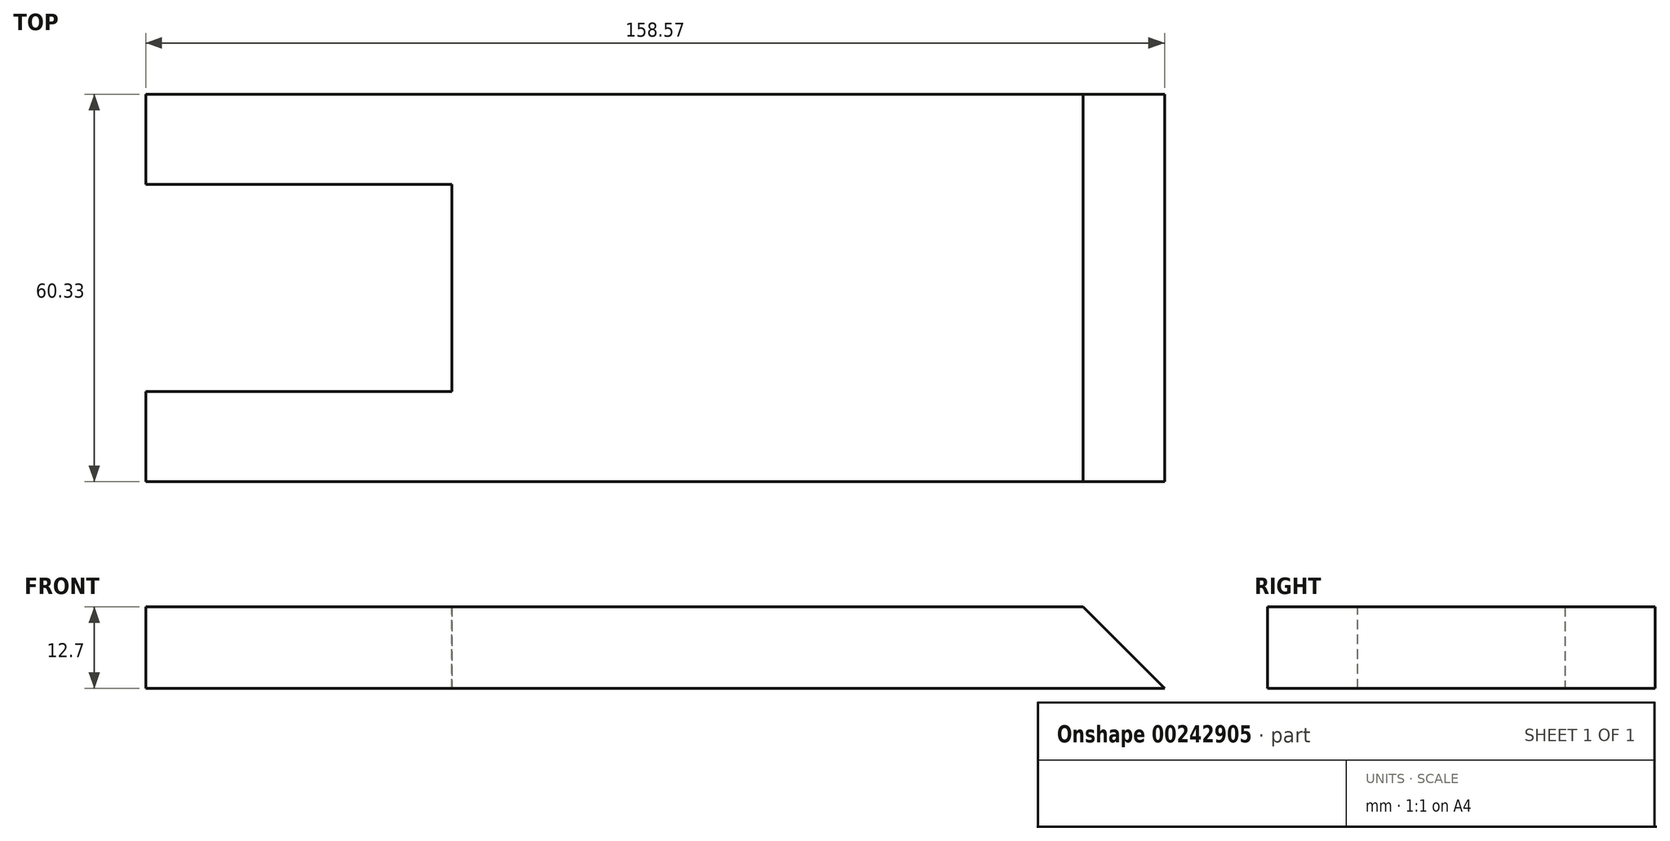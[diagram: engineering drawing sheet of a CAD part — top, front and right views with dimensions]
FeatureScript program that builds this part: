
annotation { "Feature Type Name" : "Feature", "Feature Type Description" : "" }
export const myFeature = defineFeature(function(context is Context, id is Id, definition is map)
    precondition{}
    {
        {
            var Q0;
            Q0=qCreatedBy(makeId("Top.planeOp"),FACE);
            var sketch = newSketch(context, id + "F0", { "sketchPlane" : qUnion([Q0])});
            skLineSegment(sketch, "E0", {"start": v(0, 0) * mm, "end": v(0, 14.3) * mm});
            skLineSegment(sketch, "E1", {"start": v(0, 14.3) * mm, "end": v(47.63, 14.3) * mm});
            skLineSegment(sketch, "E2", {"start": v(47.63, 14.3) * mm, "end": v(47.63, 46.04) * mm});
            skLineSegment(sketch, "E3", {"start": v(47.63, 46.04) * mm, "end": v(0, 46.04) * mm});
            skLineSegment(sketch, "E4", {"start": v(0, 46.04) * mm, "end": v(0, 60.33) * mm});
            skLineSegment(sketch, "E5", {"start": v(0, 60.33) * mm, "end": v(158.57, 60.33) * mm});
            skLineSegment(sketch, "E6", {"start": v(158.57, 60.33) * mm, "end": v(158.57, 0) * mm});
            skLineSegment(sketch, "E7", {"start": v(158.57, 0) * mm, "end": v(0, 0) * mm});
            skSolve(sketch);
        }
        {
            var Q0;
            Q0 = qSketchRegion(id + "F0", true);
            extrude(context, id + "F1", {"entities" : qUnion([Q0]), "depth" : 12.7 * mm});
        }
        {
            var Q0;
            Q0=makeQuery(id+"F1.opExtrude","SWEPT_FACE",FACE,{"disambiguationData":[OSD([sQuery(id+"F0.wireOp",EDGE,"E5")])]});
            var sketch = newSketch(context, id + "F2", { "sketchPlane" : qUnion([Q0])});
            skLineSegment(sketch, "E8", {"start": v(-158.57, 0) * mm, "end": v(-145.87, 12.7) * mm});
            skLineSegment(sketch, "E9", {"start": v(-145.87, 12.7) * mm, "end": v(-158.57, 12.7) * mm});
            skLineSegment(sketch, "E10", {"start": v(-158.57, 12.7) * mm, "end": v(-158.57, 0) * mm});
            skSolve(sketch);
        }
        {
            var Q0;
            Q0=makeQuery(id+"F2.imprint","IMPRINT",FACE,{"disambiguationData":[TD([[makeQuery(id+"F2.imprint","IMPRINT",EDGE,{"derivedFrom":sQuery(id+"F2.wireOp",EDGE,"E8")}),1.0]])]});
            extrude(context, id + "F3", {"entities" : qUnion([Q0]), "operationType" : NewBodyOperationType.REMOVE, "oppositeDirection" : true, "depth" : 76.2 * mm});
        }
        {
            var Q0;
            Q0=makeQuery(id+"F1.opExtrude","SWEPT_FACE",FACE,{"disambiguationData":[OSD([sQuery(id+"F0.wireOp",EDGE,"E4")])]});
            var sketch = newSketch(context, id + "F4", { "sketchPlane" : qUnion([Q0])});
            skLineSegment(sketch, "E11", {"start": v(-46.04, 0) * mm, "end": v(-46.04, 12.7) * mm});
            skLineSegment(sketch, "E12", {"start": v(-46.04, 12.7) * mm, "end": v(-46.3, 12.7) * mm});
            skLineSegment(sketch, "E13", {"start": v(-46.3, 12.7) * mm, "end": v(-46.3, 0) * mm});
            skLineSegment(sketch, "E14", {"start": v(-46.3, 0) * mm, "end": v(-46.04, 0) * mm});
            skSolve(sketch);
        }
        {
            var Q0;
            Q0=makeQuery(id+"F4.imprint","IMPRINT",FACE,{"disambiguationData":[TD([[makeQuery(id+"F4.imprint","IMPRINT",EDGE,{"derivedFrom":sQuery(id+"F4.wireOp",EDGE,"E11")}),-1.0]])]});
            extrude(context, id + "F5", {"entities" : qUnion([Q0]), "operationType" : NewBodyOperationType.REMOVE, "oppositeDirection" : true, "depth" : 47.62 * mm});
        }
        {
            var Q0;
            Q0=makeQuery(id+"F1.opExtrude","SWEPT_FACE",FACE,{"disambiguationData":[OSD([sQuery(id+"F0.wireOp",EDGE,"E0")])]});
            var sketch = newSketch(context, id + "F6", { "sketchPlane" : qUnion([Q0])});
            skLineSegment(sketch, "E15", {"start": v(-14.3, 0) * mm, "end": v(-14.04, 0) * mm});
            skLineSegment(sketch, "E16", {"start": v(-14.04, 0) * mm, "end": v(-14.04, 12.7) * mm});
            skLineSegment(sketch, "E17", {"start": v(-14.04, 12.7) * mm, "end": v(-14.3, 12.7) * mm});
            skLineSegment(sketch, "E18", {"start": v(-14.3, 12.7) * mm, "end": v(-14.3, 0) * mm});
            skSolve(sketch);
        }
        {
            var Q0;
            Q0=makeQuery(id+"F6.imprint","IMPRINT",FACE,{"disambiguationData":[TD([[makeQuery(id+"F6.imprint","IMPRINT",EDGE,{"derivedFrom":sQuery(id+"F6.wireOp",EDGE,"E15")}),-1.0]])]});
            extrude(context, id + "F7", {"entities" : qUnion([Q0]), "operationType" : NewBodyOperationType.REMOVE, "oppositeDirection" : true, "depth" : 47.62 * mm});
        }
    });
